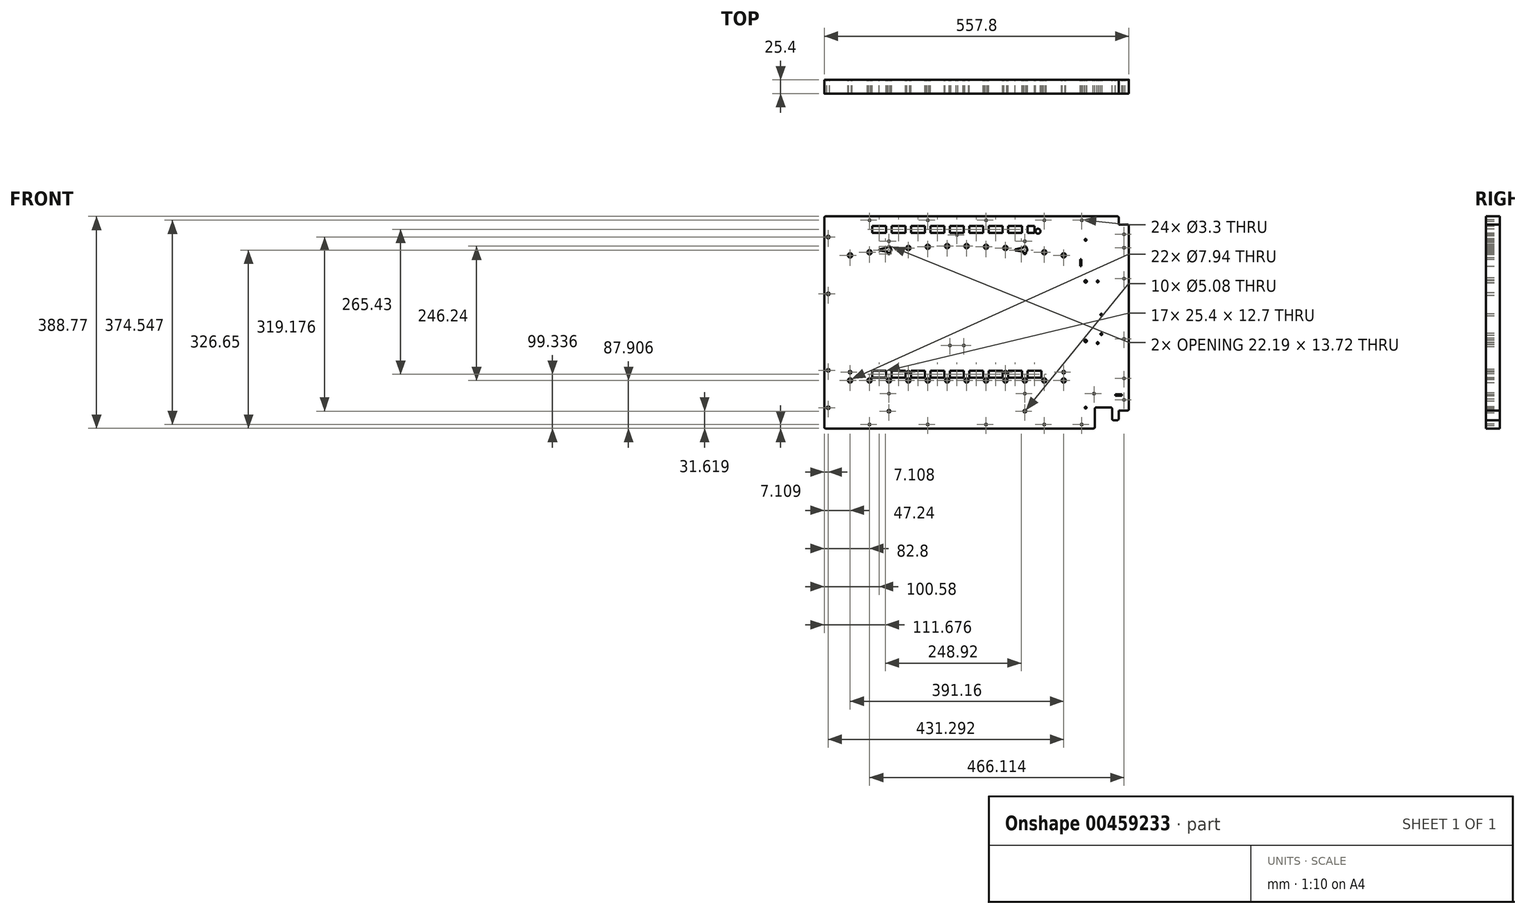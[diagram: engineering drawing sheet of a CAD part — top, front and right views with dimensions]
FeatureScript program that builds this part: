
annotation { "Feature Type Name" : "Feature", "Feature Type Description" : "" }
export const myFeature = defineFeature(function(context is Context, id is Id, definition is map)
    precondition{}
    {
        {
            var Q0;
            Q0=qCreatedBy(makeId("Front.planeOp"),FACE);
            var sketch = newSketch(context, id + "F0", { "sketchPlane" : qUnion([Q0])});
            skCircle(sketch, "E0", {"center": v(270.01, 168.97) * mm, "radius": 1.65 * mm});
            skCircle(sketch, "E1", {"center": v(270.01, 144.35) * mm, "radius": 1.65 * mm});
            skCircle(sketch, "E2", {"center": v(270.01, 87.69) * mm, "radius": 1.65 * mm});
            skCircle(sketch, "E3", {"center": v(270.01, -22.8) * mm, "radius": 1.65 * mm});
            skCircle(sketch, "E4", {"center": v(270.01, -134.56) * mm, "radius": 1.65 * mm});
            skCircle(sketch, "E5", {"center": v(270.01, -95.2) * mm, "radius": 1.65 * mm});
            skCircle(sketch, "E6", {"center": v(-196.1, -179.8) * mm, "radius": 1.65 * mm});
            skCircle(sketch, "E7", {"center": v(-89.42, -179.8) * mm, "radius": 1.65 * mm});
            skCircle(sketch, "E8", {"center": v(17.26, -179.8) * mm, "radius": 1.65 * mm});
            skCircle(sketch, "E9", {"center": v(123.94, -179.8) * mm, "radius": 1.65 * mm});
            skCircle(sketch, "E10", {"center": v(192.52, -179.8) * mm, "radius": 1.65 * mm});
            skCircle(sketch, "E11", {"center": v(-196.1, 194.75) * mm, "radius": 1.65 * mm});
            skCircle(sketch, "E12", {"center": v(-89.42, 194.75) * mm, "radius": 1.65 * mm});
            skCircle(sketch, "E13", {"center": v(17.26, 194.75) * mm, "radius": 1.65 * mm});
            skCircle(sketch, "E14", {"center": v(123.94, 194.75) * mm, "radius": 1.65 * mm});
            skCircle(sketch, "E15", {"center": v(192.52, 194.75) * mm, "radius": 1.65 * mm});
            skCircle(sketch, "E16", {"center": v(-196.1, 136) * mm, "radius": 3.97 * mm});
            skCircle(sketch, "E17", {"center": v(-124.98, 143.87) * mm, "radius": 3.97 * mm});
            skCircle(sketch, "E18", {"center": v(-89.42, 146.12) * mm, "radius": 3.97 * mm});
            skCircle(sketch, "E19", {"center": v(-53.86, 147.24) * mm, "radius": 3.97 * mm});
            skCircle(sketch, "E20", {"center": v(17.26, 146.12) * mm, "radius": 3.97 * mm});
            skCircle(sketch, "E21", {"center": v(-18.3, 147.24) * mm, "radius": 3.97 * mm});
            skCircle(sketch, "E22", {"center": v(52.82, 143.87) * mm, "radius": 3.97 * mm});
            skCircle(sketch, "E23", {"center": v(123.94, 136) * mm, "radius": 3.97 * mm});
            skCircle(sketch, "E24", {"center": v(-196.1, -99) * mm, "radius": 3.97 * mm});
            skCircle(sketch, "E25", {"center": v(-160.54, -99) * mm, "radius": 3.97 * mm});
            skCircle(sketch, "E26", {"center": v(-124.98, -99) * mm, "radius": 3.97 * mm});
            skCircle(sketch, "E27", {"center": v(-89.42, -99) * mm, "radius": 3.97 * mm});
            skCircle(sketch, "E28", {"center": v(-53.86, -99) * mm, "radius": 3.97 * mm});
            skCircle(sketch, "E29", {"center": v(-18.3, -99) * mm, "radius": 3.97 * mm});
            skCircle(sketch, "E30", {"center": v(17.26, -99) * mm, "radius": 3.97 * mm});
            skCircle(sketch, "E31", {"center": v(52.82, -99) * mm, "radius": 3.97 * mm});
            skCircle(sketch, "E32", {"center": v(88.38, -99) * mm, "radius": 3.97 * mm});
            skCircle(sketch, "E33", {"center": v(123.94, -99) * mm, "radius": 3.97 * mm});
            skCircle(sketch, "E34", {"center": v(159.5, 130.33) * mm, "radius": 3.97 * mm});
            skCircle(sketch, "E35", {"center": v(159.5, -99) * mm, "radius": 3.97 * mm});
            skCircle(sketch, "E36", {"center": v(-231.66, -99) * mm, "radius": 3.97 * mm});
            skCircle(sketch, "E37", {"center": v(-231.66, 130.33) * mm, "radius": 3.97 * mm});
            skCircle(sketch, "E38", {"center": v(-271.8, 163.89) * mm, "radius": 2.54 * mm});
            skCircle(sketch, "E39", {"center": v(-271.8, 59.75) * mm, "radius": 2.54 * mm});
            skCircle(sketch, "E40", {"center": v(-271.8, -148.94) * mm, "radius": 2.54 * mm});
            skCircle(sketch, "E41", {"center": v(-160.54, 156.27) * mm, "radius": 1.65 * mm});
            skCircle(sketch, "E42", {"center": v(88.38, 156.27) * mm, "radius": 1.65 * mm});
            skCircle(sketch, "E43", {"center": v(-36.08, 167.95) * mm, "radius": 1.65 * mm});
            skCircle(sketch, "E44", {"center": v(199.63, 82.6) * mm, "radius": 2.29 * mm});
            skCircle(sketch, "E45", {"center": v(221.73, 82.6) * mm, "radius": 1.66 * mm});
            skCircle(sketch, "E46", {"center": v(199.63, -26.61) * mm, "radius": 2.29 * mm});
            skCircle(sketch, "E47", {"center": v(221.73, -30.42) * mm, "radius": 1.66 * mm});
            skCircle(sketch, "E48", {"center": v(-160.54, -155.3) * mm, "radius": 2.54 * mm});
            skCircle(sketch, "E49", {"center": v(88.38, -155.3) * mm, "radius": 2.54 * mm});
            skCircle(sketch, "E50", {"center": v(-231.66, -83.76) * mm, "radius": 2.54 * mm});
            skCircle(sketch, "E51", {"center": v(159.5, -83.76) * mm, "radius": 2.54 * mm});
            skCircle(sketch, "E52", {"center": v(-160.54, -123.13) * mm, "radius": 1.65 * mm});
            skCircle(sketch, "E53", {"center": v(88.38, -123.13) * mm, "radius": 1.65 * mm});
            skCircle(sketch, "E54", {"center": v(-271.8, -80.36) * mm, "radius": 2.54 * mm});
            skCircle(sketch, "E55", {"center": v(-124.98, -83.76) * mm, "radius": 2.54 * mm});
            skCircle(sketch, "E56", {"center": v(52.82, -83.76) * mm, "radius": 2.54 * mm});
            skCircle(sketch, "E57", {"center": v(228.49, -13.91) * mm, "radius": 1.66 * mm});
            skCircle(sketch, "E58", {"center": v(228.49, 21.65) * mm, "radius": 1.66 * mm});
            skCircle(sketch, "E59", {"center": v(112.5, 174.6) * mm, "radius": 4.45 * mm});
            skCircle(sketch, "E60", {"center": v(199.63, 158.8) * mm, "radius": 1.66 * mm});
            skCircle(sketch, "E61", {"center": v(199.63, -148.94) * mm, "radius": 1.66 * mm});
            skCircle(sketch, "E62", {"center": v(-48.78, -34.87) * mm, "radius": 1.65 * mm});
            skCircle(sketch, "E63", {"center": v(-23.38, -34.87) * mm, "radius": 1.65 * mm});
            skCircle(sketch, "E64", {"center": v(214.97, -123.13) * mm, "radius": 1.65 * mm});
            skLineSegment(sketch, "E65", {"start": v(-48.78, 171.5) * mm, "end": v(-23.38, 171.5) * mm});
            skLineSegment(sketch, "E66", {"start": v(-23.38, 171.5) * mm, "end": v(-23.38, 184.2) * mm});
            skLineSegment(sketch, "E67", {"start": v(-23.38, 184.2) * mm, "end": v(-48.78, 184.2) * mm});
            skLineSegment(sketch, "E68", {"start": v(-48.78, 184.2) * mm, "end": v(-48.78, 171.5) * mm});
            skLineSegment(sketch, "E69", {"start": v(-58.94, 184.2) * mm, "end": v(-84.34, 184.2) * mm});
            skLineSegment(sketch, "E70", {"start": v(-84.34, 184.2) * mm, "end": v(-84.34, 171.5) * mm});
            skLineSegment(sketch, "E71", {"start": v(-84.34, 171.5) * mm, "end": v(-58.94, 171.5) * mm});
            skLineSegment(sketch, "E72", {"start": v(-58.94, 171.5) * mm, "end": v(-58.94, 184.2) * mm});
            skLineSegment(sketch, "E73", {"start": v(-94.5, 184.2) * mm, "end": v(-119.9, 184.2) * mm});
            skLineSegment(sketch, "E74", {"start": v(-119.9, 184.2) * mm, "end": v(-119.9, 171.5) * mm});
            skLineSegment(sketch, "E75", {"start": v(-119.9, 171.5) * mm, "end": v(-94.5, 171.5) * mm});
            skLineSegment(sketch, "E76", {"start": v(-94.5, 171.5) * mm, "end": v(-94.5, 184.2) * mm});
            skLineSegment(sketch, "E77", {"start": v(-130.06, 184.2) * mm, "end": v(-155.46, 184.2) * mm});
            skLineSegment(sketch, "E78", {"start": v(-155.46, 184.2) * mm, "end": v(-155.46, 171.5) * mm});
            skLineSegment(sketch, "E79", {"start": v(-155.46, 171.5) * mm, "end": v(-130.06, 171.5) * mm});
            skLineSegment(sketch, "E80", {"start": v(-130.06, 171.5) * mm, "end": v(-130.06, 184.2) * mm});
            skLineSegment(sketch, "E81", {"start": v(-165.62, 184.2) * mm, "end": v(-191.02, 184.2) * mm});
            skLineSegment(sketch, "E82", {"start": v(-191.02, 184.2) * mm, "end": v(-191.02, 171.5) * mm});
            skLineSegment(sketch, "E83", {"start": v(-191.02, 171.5) * mm, "end": v(-165.62, 171.5) * mm});
            skLineSegment(sketch, "E84", {"start": v(-165.62, 171.5) * mm, "end": v(-165.62, 184.2) * mm});
            skLineSegment(sketch, "E85", {"start": v(-13.22, 171.5) * mm, "end": v(12.18, 171.5) * mm});
            skLineSegment(sketch, "E86", {"start": v(12.18, 171.5) * mm, "end": v(12.18, 184.2) * mm});
            skLineSegment(sketch, "E87", {"start": v(12.18, 184.2) * mm, "end": v(-13.22, 184.2) * mm});
            skLineSegment(sketch, "E88", {"start": v(-13.22, 184.2) * mm, "end": v(-13.22, 171.5) * mm});
            skLineSegment(sketch, "E89", {"start": v(22.34, 171.5) * mm, "end": v(47.74, 171.5) * mm});
            skLineSegment(sketch, "E90", {"start": v(47.74, 171.5) * mm, "end": v(47.74, 184.2) * mm});
            skLineSegment(sketch, "E91", {"start": v(47.74, 184.2) * mm, "end": v(22.34, 184.2) * mm});
            skLineSegment(sketch, "E92", {"start": v(22.34, 184.2) * mm, "end": v(22.34, 171.5) * mm});
            skLineSegment(sketch, "E93", {"start": v(57.9, 171.5) * mm, "end": v(83.3, 171.5) * mm});
            skLineSegment(sketch, "E94", {"start": v(83.3, 171.5) * mm, "end": v(83.3, 184.2) * mm});
            skLineSegment(sketch, "E95", {"start": v(83.3, 184.2) * mm, "end": v(57.9, 184.2) * mm});
            skLineSegment(sketch, "E96", {"start": v(57.9, 184.2) * mm, "end": v(57.9, 171.5) * mm});
            skLineSegment(sketch, "E97", {"start": v(93.46, 171.5) * mm, "end": v(106.16, 171.5) * mm});
            skLineSegment(sketch, "E98", {"start": v(106.16, 171.5) * mm, "end": v(106.16, 184.2) * mm});
            skLineSegment(sketch, "E99", {"start": v(106.16, 184.2) * mm, "end": v(93.46, 184.2) * mm});
            skLineSegment(sketch, "E100", {"start": v(93.46, 184.2) * mm, "end": v(93.46, 171.5) * mm});
            skLineSegment(sketch, "E101", {"start": v(-48.78, -93.92) * mm, "end": v(-23.38, -93.92) * mm});
            skLineSegment(sketch, "E102", {"start": v(-23.38, -93.92) * mm, "end": v(-23.38, -81.22) * mm});
            skLineSegment(sketch, "E103", {"start": v(-23.38, -81.22) * mm, "end": v(-48.78, -81.22) * mm});
            skLineSegment(sketch, "E104", {"start": v(-48.78, -81.22) * mm, "end": v(-48.78, -93.92) * mm});
            skLineSegment(sketch, "E105", {"start": v(-58.94, -81.22) * mm, "end": v(-84.34, -81.22) * mm});
            skLineSegment(sketch, "E106", {"start": v(-84.34, -81.22) * mm, "end": v(-84.34, -93.92) * mm});
            skLineSegment(sketch, "E107", {"start": v(-84.34, -93.92) * mm, "end": v(-58.94, -93.92) * mm});
            skLineSegment(sketch, "E108", {"start": v(-58.94, -93.92) * mm, "end": v(-58.94, -81.22) * mm});
            skLineSegment(sketch, "E109", {"start": v(-94.5, -81.22) * mm, "end": v(-119.9, -81.22) * mm});
            skLineSegment(sketch, "E110", {"start": v(-119.9, -81.22) * mm, "end": v(-119.9, -93.92) * mm});
            skLineSegment(sketch, "E111", {"start": v(-119.9, -93.92) * mm, "end": v(-94.5, -93.92) * mm});
            skLineSegment(sketch, "E112", {"start": v(-94.5, -93.92) * mm, "end": v(-94.5, -81.22) * mm});
            skLineSegment(sketch, "E113", {"start": v(-130.06, -81.22) * mm, "end": v(-155.46, -81.22) * mm});
            skLineSegment(sketch, "E114", {"start": v(-155.46, -81.22) * mm, "end": v(-155.46, -93.92) * mm});
            skLineSegment(sketch, "E115", {"start": v(-155.46, -93.92) * mm, "end": v(-130.06, -93.92) * mm});
            skLineSegment(sketch, "E116", {"start": v(-130.06, -93.92) * mm, "end": v(-130.06, -81.22) * mm});
            skLineSegment(sketch, "E117", {"start": v(-165.62, -81.22) * mm, "end": v(-191.02, -81.22) * mm});
            skLineSegment(sketch, "E118", {"start": v(-191.02, -81.22) * mm, "end": v(-191.02, -93.92) * mm});
            skLineSegment(sketch, "E119", {"start": v(-191.02, -93.92) * mm, "end": v(-165.62, -93.92) * mm});
            skLineSegment(sketch, "E120", {"start": v(-165.62, -93.92) * mm, "end": v(-165.62, -81.22) * mm});
            skLineSegment(sketch, "E121", {"start": v(-13.22, -93.92) * mm, "end": v(12.18, -93.92) * mm});
            skLineSegment(sketch, "E122", {"start": v(12.18, -93.92) * mm, "end": v(12.18, -81.22) * mm});
            skLineSegment(sketch, "E123", {"start": v(12.18, -81.22) * mm, "end": v(-13.22, -81.22) * mm});
            skLineSegment(sketch, "E124", {"start": v(-13.22, -81.22) * mm, "end": v(-13.22, -93.92) * mm});
            skLineSegment(sketch, "E125", {"start": v(22.34, -93.92) * mm, "end": v(47.74, -93.92) * mm});
            skLineSegment(sketch, "E126", {"start": v(47.74, -93.92) * mm, "end": v(47.74, -81.22) * mm});
            skLineSegment(sketch, "E127", {"start": v(47.74, -81.22) * mm, "end": v(22.34, -81.22) * mm});
            skLineSegment(sketch, "E128", {"start": v(22.34, -81.22) * mm, "end": v(22.34, -93.92) * mm});
            skLineSegment(sketch, "E129", {"start": v(57.9, -93.92) * mm, "end": v(83.3, -93.92) * mm});
            skLineSegment(sketch, "E130", {"start": v(83.3, -93.92) * mm, "end": v(83.3, -81.22) * mm});
            skLineSegment(sketch, "E131", {"start": v(83.3, -81.22) * mm, "end": v(57.9, -81.22) * mm});
            skLineSegment(sketch, "E132", {"start": v(57.9, -81.22) * mm, "end": v(57.9, -93.92) * mm});
            skLineSegment(sketch, "E133", {"start": v(93.46, -93.92) * mm, "end": v(118.86, -93.92) * mm});
            skLineSegment(sketch, "E134", {"start": v(118.86, -93.92) * mm, "end": v(118.86, -81.22) * mm});
            skLineSegment(sketch, "E135", {"start": v(118.86, -81.22) * mm, "end": v(93.46, -81.22) * mm});
            skLineSegment(sketch, "E136", {"start": v(93.46, -81.22) * mm, "end": v(93.46, -93.92) * mm});
            skLineSegment(sketch, "E137", {"start": v(-163.33, 145.92) * mm, "end": v(-163.33, 144.06) * mm});
            skLineSegment(sketch, "E138", {"start": v(-163.33, 144.06) * mm, "end": v(-165.62, 144.06) * mm});
            skLineSegment(sketch, "E139", {"start": v(-165.62, 144.06) * mm, "end": v(-177.3, 141.75) * mm});
            skLineSegment(sketch, "E140", {"start": v(-177.3, 139.26) * mm, "end": v(-165.62, 136.95) * mm});
            skLineSegment(sketch, "E141", {"start": v(-165.62, 136.95) * mm, "end": v(-163.2, 136.95) * mm});
            skLineSegment(sketch, "E142", {"start": v(-162.32, 136.43) * mm, "end": v(-162.32, 133.1) * mm});
            skLineSegment(sketch, "E143", {"start": v(-158.76, 133.1) * mm, "end": v(-158.76, 136.43) * mm});
            skLineSegment(sketch, "E144", {"start": v(-157.75, 143.96) * mm, "end": v(-157.75, 145.92) * mm});
            skLineSegment(sketch, "E145", {"start": v(85.59, 145.92) * mm, "end": v(85.59, 144.06) * mm});
            skLineSegment(sketch, "E146", {"start": v(85.59, 144.06) * mm, "end": v(83.3, 144.06) * mm});
            skLineSegment(sketch, "E147", {"start": v(83.3, 144.06) * mm, "end": v(71.62, 141.75) * mm});
            skLineSegment(sketch, "E148", {"start": v(71.62, 139.26) * mm, "end": v(83.3, 136.95) * mm});
            skLineSegment(sketch, "E149", {"start": v(83.3, 136.95) * mm, "end": v(85.71, 136.95) * mm});
            skLineSegment(sketch, "E150", {"start": v(86.6, 136.43) * mm, "end": v(86.6, 133.1) * mm});
            skLineSegment(sketch, "E151", {"start": v(90.16, 133.1) * mm, "end": v(90.16, 136.43) * mm});
            skLineSegment(sketch, "E152", {"start": v(91.17, 143.96) * mm, "end": v(91.17, 145.92) * mm});
            skLineSegment(sketch, "E153", {"start": v(189.95, 110.55) * mm, "end": v(191.63, 110.55) * mm});
            skLineSegment(sketch, "E154", {"start": v(191.63, 110.55) * mm, "end": v(191.63, 123.25) * mm});
            skLineSegment(sketch, "E155", {"start": v(191.63, 123.25) * mm, "end": v(189.95, 123.25) * mm});
            skLineSegment(sketch, "E156", {"start": v(189.95, 123.25) * mm, "end": v(189.95, 110.55) * mm});
            skLineSegment(sketch, "E157", {"start": v(253.89, -124.4) * mm, "end": v(253.89, -126.94) * mm});
            skLineSegment(sketch, "E158", {"start": v(253.89, -126.94) * mm, "end": v(266.2, -126.94) * mm});
            skLineSegment(sketch, "E159", {"start": v(266.2, -126.94) * mm, "end": v(266.2, -124.4) * mm});
            skLineSegment(sketch, "E160", {"start": v(266.2, -124.4) * mm, "end": v(253.89, -124.4) * mm});
            skLineSegment(sketch, "E161", {"start": v(278.9, -151.48) * mm, "end": v(278.9, 184.2) * mm});
            skLineSegment(sketch, "E162", {"start": v(260.24, -154.02) * mm, "end": v(276.36, -154.02) * mm});
            skLineSegment(sketch, "E163", {"start": v(260.24, -169.26) * mm, "end": v(260.24, -154.02) * mm});
            skLineSegment(sketch, "E164", {"start": v(250.58, -171.8) * mm, "end": v(257.7, -171.8) * mm});
            skLineSegment(sketch, "E165", {"start": v(248.04, -150.97) * mm, "end": v(248.04, -169.26) * mm});
            skLineSegment(sketch, "E166", {"start": v(219.09, -148.43) * mm, "end": v(245.5, -148.43) * mm});
            skLineSegment(sketch, "E167", {"start": v(216.55, -184.37) * mm, "end": v(216.55, -150.97) * mm});
            skLineSegment(sketch, "E168", {"start": v(-276.36, -186.91) * mm, "end": v(214, -186.91) * mm});
            skLineSegment(sketch, "E169", {"start": v(-278.9, 199.32) * mm, "end": v(-278.9, -184.37) * mm});
            skLineSegment(sketch, "E170", {"start": v(257.7, 201.86) * mm, "end": v(-276.36, 201.86) * mm});
            skLineSegment(sketch, "E171", {"start": v(260.24, 186.75) * mm, "end": v(260.24, 199.32) * mm});
            skLineSegment(sketch, "E172", {"start": v(276.36, 186.75) * mm, "end": v(260.24, 186.75) * mm});
            skArc(sketch, "E173", {"start": v(-177.3, 141.75) * mm, "mid": v(-178.32, 140.5) * mm, "end": v(-177.3, 139.26) * mm});
            skArc(sketch, "E174", {"start": v(-163.2, 136.95) * mm, "mid": v(-162.78, 136.66) * mm, "end": v(-162.32, 136.43) * mm});
            skArc(sketch, "E175", {"start": v(-162.32, 133.1) * mm, "mid": v(-160.54, 132.88) * mm, "end": v(-158.76, 133.1) * mm});
            skArc(sketch, "E176", {"start": v(-158.76, 136.43) * mm, "mid": v(-156.14, 139.9) * mm, "end": v(-157.75, 143.96) * mm});
            skArc(sketch, "E177", {"start": v(-157.75, 145.92) * mm, "mid": v(-160.54, 146.6) * mm, "end": v(-163.33, 145.92) * mm});
            skArc(sketch, "E178", {"start": v(71.62, 141.75) * mm, "mid": v(70.6, 140.5) * mm, "end": v(71.62, 139.26) * mm});
            skArc(sketch, "E179", {"start": v(85.71, 136.95) * mm, "mid": v(86.14, 136.66) * mm, "end": v(86.6, 136.43) * mm});
            skArc(sketch, "E180", {"start": v(86.6, 133.1) * mm, "mid": v(88.38, 132.88) * mm, "end": v(90.16, 133.1) * mm});
            skArc(sketch, "E181", {"start": v(90.16, 136.43) * mm, "mid": v(92.78, 139.9) * mm, "end": v(91.17, 143.96) * mm});
            skArc(sketch, "E182", {"start": v(91.17, 145.92) * mm, "mid": v(88.38, 146.6) * mm, "end": v(85.59, 145.92) * mm});
            skArc(sketch, "E183", {"start": v(276.36, -154.02) * mm, "mid": v(278.16, -153.28) * mm, "end": v(278.9, -151.48) * mm});
            skArc(sketch, "E184", {"start": v(257.7, -171.8) * mm, "mid": v(259.5, -171.06) * mm, "end": v(260.24, -169.26) * mm});
            skArc(sketch, "E185", {"start": v(248.04, -169.26) * mm, "mid": v(248.79, -171.06) * mm, "end": v(250.58, -171.8) * mm});
            skArc(sketch, "E186", {"start": v(248.04, -150.97) * mm, "mid": v(247.3, -149.18) * mm, "end": v(245.5, -148.43) * mm});
            skArc(sketch, "E187", {"start": v(219.09, -148.43) * mm, "mid": v(217.3, -149.18) * mm, "end": v(216.55, -150.97) * mm});
            skArc(sketch, "E188", {"start": v(214, -186.91) * mm, "mid": v(215.8, -186.17) * mm, "end": v(216.55, -184.37) * mm});
            skArc(sketch, "E189", {"start": v(-278.9, -184.37) * mm, "mid": v(-278.16, -186.17) * mm, "end": v(-276.36, -186.91) * mm});
            skArc(sketch, "E190", {"start": v(-276.36, 201.86) * mm, "mid": v(-278.16, 201.11) * mm, "end": v(-278.9, 199.32) * mm});
            skArc(sketch, "E191", {"start": v(260.24, 199.32) * mm, "mid": v(259.5, 201.11) * mm, "end": v(257.7, 201.86) * mm});
            skArc(sketch, "E192", {"start": v(278.9, 184.2) * mm, "mid": v(278.16, 186) * mm, "end": v(276.36, 186.75) * mm});
            skSolve(sketch);
        }
        {
            var Q0;
            Q0=qSketchRegion(id+"F0",true);
            extrude(context, id + "F1", {"entities" : qUnion([Q0]), "depth" : 25.4 * mm});
        }
    });
